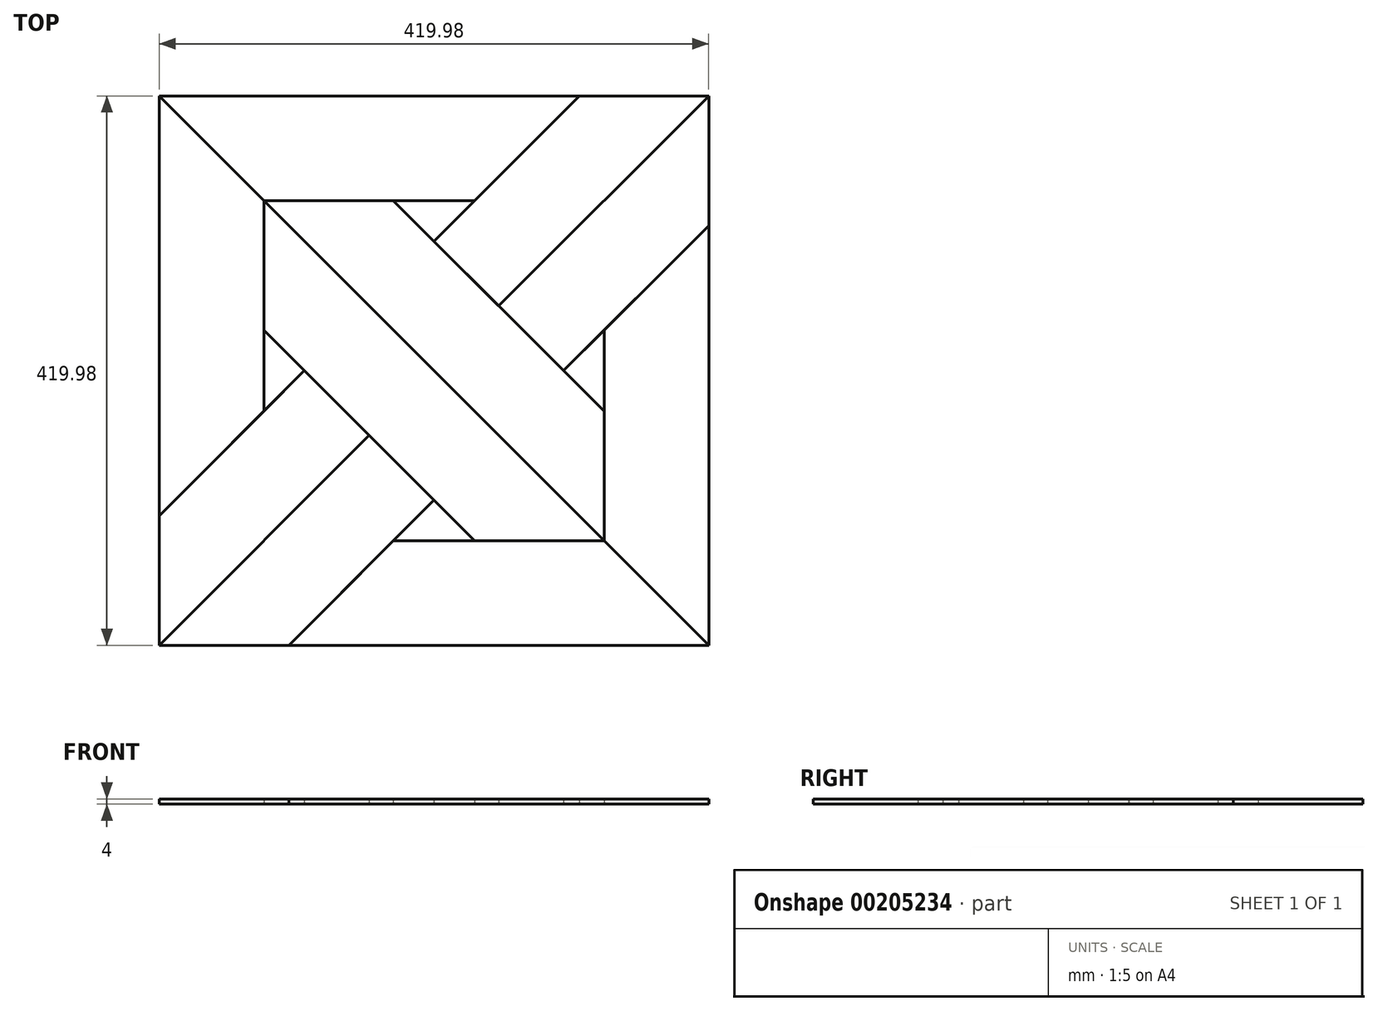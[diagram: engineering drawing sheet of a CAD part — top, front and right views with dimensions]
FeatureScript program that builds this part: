
annotation { "Feature Type Name" : "Feature", "Feature Type Description" : "" }
export const myFeature = defineFeature(function(context is Context, id is Id, definition is map)
    precondition{}
    {
        {
            assignVariable(context, id + "F0", {"name" : "panel_thickness", "anyValue" : 4 * mm});
        }
        {
            var Q0;
            Q0=qCreatedBy(makeId("Top.planeOp"),FACE);
            var sketch = newSketch(context, id + "F1", { "sketchPlane" : qUnion([Q0])});
            skLineSegment(sketch, "E0", {"start": v(0, 0) * mm, "end": v(-130, 130) * mm});
            skLineSegment(sketch, "E1", {"start": v(-130, 130) * mm, "end": v(-31.01, 130) * mm});
            skLineSegment(sketch, "E2", {"start": v(-130, 130) * mm, "end": v(-130, 31.01) * mm});
            skLineSegment(sketch, "E3", {"start": v(-31.01, 130) * mm, "end": v(31, 130) * mm});
            skLineSegment(sketch, "E4", {"start": v(-130, 31.01) * mm, "end": v(-130, -31) * mm});
            skLineSegment(sketch, "E5", {"start": v(-31.01, 130) * mm, "end": v(0, 99) * mm});
            skLineSegment(sketch, "E6", {"start": v(0, 99) * mm, "end": v(31, 130) * mm});
            skLineSegment(sketch, "E7", {"start": v(-130, 31.01) * mm, "end": v(-99, 0) * mm});
            skLineSegment(sketch, "E8", {"start": v(-99, 0) * mm, "end": v(-130, -31) * mm});
            skLineSegment(sketch, "E9", {"start": v(0, 0) * mm, "end": v(49.5, 49.5) * mm, "construction": true});
            skLineSegment(sketch, "E10", {"start": v(0, 0) * mm, "end": v(-49.5, -49.5) * mm, "construction": true});
            skLineSegment(sketch, "E11", {"start": v(-99, 0) * mm, "end": v(-49.5, -49.5) * mm});
            skLineSegment(sketch, "E12", {"start": v(0, 99) * mm, "end": v(49.5, 49.5) * mm});
            skLineSegment(sketch, "E13", {"start": v(49.5, 49.5) * mm, "end": v(210, 210) * mm});
            skLineSegment(sketch, "E14", {"start": v(-49.5, -49.5) * mm, "end": v(-210, -210) * mm});
            skLineSegment(sketch, "E15", {"start": v(210, 210) * mm, "end": v(111, 210) * mm});
            skLineSegment(sketch, "E16", {"start": v(-210, -210) * mm, "end": v(-210, -111) * mm});
            skLineSegment(sketch, "E17", {"start": v(31, 130) * mm, "end": v(111, 210) * mm});
            skLineSegment(sketch, "E18", {"start": v(-130, -31) * mm, "end": v(-210, -111) * mm});
            skLineSegment(sketch, "E19", {"start": v(111, 210) * mm, "end": v(-210, 210) * mm});
            skLineSegment(sketch, "E20", {"start": v(-210, 210) * mm, "end": v(-210, -111) * mm});
            skLineSegment(sketch, "E21", {"start": v(-130, 130) * mm, "end": v(-210, 210) * mm});
            skLineSegment(sketch, "E22.MirrorCS", {"start": v(0, 0) * mm, "end": v(130, -130) * mm});
            skLineSegment(sketch, "E23.MirrorCS", {"start": v(99, 0) * mm, "end": v(49.5, 49.5) * mm});
            skLineSegment(sketch, "E24.MirrorCS", {"start": v(130, -31.01) * mm, "end": v(99, 0) * mm});
            skLineSegment(sketch, "E25.MirrorCS", {"start": v(130, -31.01) * mm, "end": v(130, 31) * mm});
            skLineSegment(sketch, "E26.MirrorCS", {"start": v(99, 0) * mm, "end": v(130, 31) * mm});
            skLineSegment(sketch, "E27.MirrorCS", {"start": v(130, 31) * mm, "end": v(210, 111) * mm});
            skLineSegment(sketch, "E28.MirrorCS", {"start": v(210, 210) * mm, "end": v(210, 111) * mm});
            skLineSegment(sketch, "E29.MirrorCS", {"start": v(210, 111) * mm, "end": v(210, -210) * mm});
            skLineSegment(sketch, "E30.MirrorCS", {"start": v(130, -130) * mm, "end": v(210, -210) * mm});
            skLineSegment(sketch, "E31.MirrorCS", {"start": v(210, -210) * mm, "end": v(-111, -210) * mm});
            skLineSegment(sketch, "E32.MirrorCS", {"start": v(-210, -210) * mm, "end": v(-111, -210) * mm});
            skLineSegment(sketch, "E33.MirrorCS", {"start": v(0, -99) * mm, "end": v(-49.5, -49.5) * mm});
            skLineSegment(sketch, "E34.MirrorCS", {"start": v(31.01, -130) * mm, "end": v(0, -99) * mm});
            skLineSegment(sketch, "E35.MirrorCS", {"start": v(31.01, -130) * mm, "end": v(-31, -130) * mm});
            skLineSegment(sketch, "E36.MirrorCS", {"start": v(0, -99) * mm, "end": v(-31, -130) * mm});
            skLineSegment(sketch, "E37.MirrorCS", {"start": v(-31, -130) * mm, "end": v(-111, -210) * mm});
            skLineSegment(sketch, "E38.MirrorCS", {"start": v(130, -130) * mm, "end": v(31.01, -130) * mm});
            skLineSegment(sketch, "E39.MirrorCS", {"start": v(130, -130) * mm, "end": v(130, -31.01) * mm});
            skSolve(sketch);
        }
        {
            var Q0;
            Q0=makeQuery(id+"F1.imprint","IMPRINT",FACE,{"disambiguationData":[TD([[makeQuery(id+"F1.imprint","IMPRINT",EDGE,{"derivedFrom":sQuery(id+"F1.wireOp",EDGE,"E2")}),-1.0]])]});
            var Q1;
            Q1=makeQuery(id+"F1.imprint","IMPRINT",FACE,{"disambiguationData":[TD([[makeQuery(id+"F1.imprint","IMPRINT",EDGE,{"derivedFrom":sQuery(id+"F1.wireOp",EDGE,"E25.MirrorCS")}),-1.0]])]});
            var Q2;
            Q2=makeQuery(id+"F1.imprint","IMPRINT",FACE,{"disambiguationData":[TD([[makeQuery(id+"F1.imprint","IMPRINT",EDGE,{"derivedFrom":sQuery(id+"F1.wireOp",EDGE,"E14")}),1.0]])]});
            var Q3;
            Q3=makeQuery(id+"F1.imprint","IMPRINT",FACE,{"disambiguationData":[TD([[makeQuery(id+"F1.imprint","IMPRINT",EDGE,{"derivedFrom":sQuery(id+"F1.wireOp",EDGE,"E6")}),-1.0]])]});
            extrude(context, id + "F2", {"entities" : qUnion([Q0, Q1, Q2, Q3]), "depth" : getVariable(context, 'panel_thickness')});
        }
        {
            var Q0;
            Q0=makeQuery(id+"F1.imprint","IMPRINT",FACE,{"disambiguationData":[TD([[makeQuery(id+"F1.imprint","IMPRINT",EDGE,{"derivedFrom":sQuery(id+"F1.wireOp",EDGE,"E1")}),1.0]])]});
            var Q1;
            Q1=makeQuery(id+"F1.imprint","IMPRINT",FACE,{"disambiguationData":[TD([[makeQuery(id+"F1.imprint","IMPRINT",EDGE,{"derivedFrom":sQuery(id+"F1.wireOp",EDGE,"E8")}),1.0]])]});
            var Q2;
            Q2=makeQuery(id+"F1.imprint","IMPRINT",FACE,{"disambiguationData":[TD([[makeQuery(id+"F1.imprint","IMPRINT",EDGE,{"derivedFrom":sQuery(id+"F1.wireOp",EDGE,"E13")}),-1.0]])]});
            var Q3;
            Q3=makeQuery(id+"F1.imprint","IMPRINT",FACE,{"disambiguationData":[TD([[makeQuery(id+"F1.imprint","IMPRINT",EDGE,{"derivedFrom":sQuery(id+"F1.wireOp",EDGE,"E30.MirrorCS")}),-1.0]])]});
            extrude(context, id + "F3", {"entities" : qUnion([Q0, Q1, Q2, Q3]), "depth" : getVariable(context, 'panel_thickness')});
        }
        {
            var Q0;
            Q0=makeQuery(id+"F1.imprint","IMPRINT",FACE,{"disambiguationData":[TD([[makeQuery(id+"F1.imprint","IMPRINT",EDGE,{"derivedFrom":sQuery(id+"F1.wireOp",EDGE,"E0")}),1.0]])]});
            var Q1;
            Q1=makeQuery(id+"F1.imprint","IMPRINT",FACE,{"disambiguationData":[TD([[makeQuery(id+"F1.imprint","IMPRINT",EDGE,{"derivedFrom":sQuery(id+"F1.wireOp",EDGE,"E3")}),-1.0]])]});
            var Q2;
            Q2=makeQuery(id+"F1.imprint","IMPRINT",FACE,{"disambiguationData":[TD([[makeQuery(id+"F1.imprint","IMPRINT",EDGE,{"derivedFrom":sQuery(id+"F1.wireOp",EDGE,"E24.MirrorCS")}),-1.0]])]});
            extrude(context, id + "F4", {"entities" : qUnion([Q0, Q1, Q2]), "depth" : getVariable(context, 'panel_thickness')});
        }
        {
            var Q0;
            Q0=makeQuery(id+"F1.imprint","IMPRINT",FACE,{"disambiguationData":[TD([[makeQuery(id+"F1.imprint","IMPRINT",EDGE,{"derivedFrom":sQuery(id+"F1.wireOp",EDGE,"E4")}),1.0]])]});
            var Q1;
            Q1=makeQuery(id+"F1.imprint","IMPRINT",FACE,{"disambiguationData":[TD([[makeQuery(id+"F1.imprint","IMPRINT",EDGE,{"derivedFrom":sQuery(id+"F1.wireOp",EDGE,"E0")}),-1.0]])]});
            var Q2;
            Q2=makeQuery(id+"F1.imprint","IMPRINT",FACE,{"disambiguationData":[TD([[makeQuery(id+"F1.imprint","IMPRINT",EDGE,{"derivedFrom":sQuery(id+"F1.wireOp",EDGE,"E34.MirrorCS")}),1.0]])]});
            extrude(context, id + "F5", {"entities" : qUnion([Q0, Q1, Q2]), "depth" : getVariable(context, 'panel_thickness')});
        }
    });
